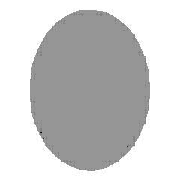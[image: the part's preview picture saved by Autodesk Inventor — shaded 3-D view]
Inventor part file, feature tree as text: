
AUTODESK INVENTOR PART (.ipt)
format: ipt  version: 2013 (Build 170138000, 138)  size: 112,640 bytes
history: native  units: mm (DEFAULTED — no unit token found)
features: other x4, plane x3, sketch x3, split x2
ambient origin geometry x8: Origin, YZ Plane, XZ Plane, XY Plane, X Axis, Y Axis, Z Axis, Center Point
bodies: Solid1 (feature_tree), Body (feature_tree)
feature tree (12):
  parser-record x1  (decoder bookkeeping rows leaked as tree rows — omitted from the tree; the rows remain in map.json)
  other  "Driven Length"
  other  "Start plane"
  other  "End plane"
  plane  "Work Plane4"
  split  "Split1"
  plane  "Work Plane5"
  split  "Split2"
  sketch  "Sketch"  dims[d2=0.0mm d4=-19.05mm d5=660.4mm d6=90.0deg d7=679.45mm]
  sketch  "Sketch2"  dims[d0=38.1mm]
  plane  "Work Plane3"
  sketch  "Sketch3"  dims[d1=679.45mm]
